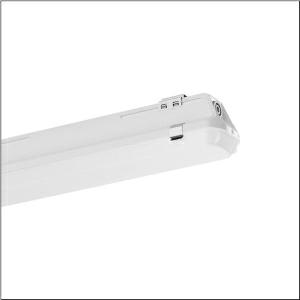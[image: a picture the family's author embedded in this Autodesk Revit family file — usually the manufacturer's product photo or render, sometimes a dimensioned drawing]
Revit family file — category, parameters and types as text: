
# Revit family: monsun_r__21_parking_51fg20dp440b_2f1b
name_source: partatom
category: Lighting Fixtures
units: mm (PartAtom-declared; Revit-internal decimal feet)

## family parameters
Cut with Voids When Loaded = No
Host = Face
Light Source = No
Part Type = Normal
Room Calculation Point = No
Round Connector Dimension = Use Diameter
Shared = No

## types (1)
- --- (1 x LED, 4810 lm, 34.4 W, 4000K)
    Apparent Load = 34 VA
    CIE Flux Codes = 45 75 93 94 100
    Color Rendering = 80
    Color Temperature = 4000K
    Default Elevation = 1800 mm
    Description = Monsun® 21 parking, damp-proof luminaire, chain hanger, primary optical cover: enclosure, of PC, light emission: direct distribution, primary light characteristic: symmetric, installation type: suspended mounting, surface-mounted, horizontal mounting, vertical mounting, LED, rated luminous flux: 4.810lm, luminous efficacy: 140lm/W, light colour: 840, colour temperature: 4000K, control gear: ECG DALI, with terminal, 5-pole, max. 2.5mm², mains connection: 220..240V, AC, 50/60Hz, rated input power: 34W, housing, of glass-fibre reinforced polyester, uncoated, bright grey, incl. chain hanger, length: 1.590mm, width: 90mm, height: 88mm, clip for enclosure, of stainless steel (V2A), ceiling mounting element, of stainless steel (V2A), chain hanger, of stainless steel (V2A), protection rating (complete): IP66, insulation class (complete): insulation class I (protective earthing), certification: CE, ENEC, VDE, UKCA, protection symbol: D, impact resistance: IK08, permissible operating ambient temperature: -25..+35°C, standard: EN 50419, EN 60598-2-1, corresponds to IFS (International Featured Standards) requirements for safety and quality in the food industry, for indoor or canopied outdoor use, no direct snow, no direct sun, no direct rain, contact your sales advisor before using the luminaires in applications with unclear chemical exposure, large temperature fluctuations or condensation-forming humidity, LABS conformity tested according to VDMA 24364:2018-05, packaging unit: 1 piece
    Height = 89 mm
    Lamp = 1 x LED
    Lamp Light Flux = 4810 lm
    Lamp Power = 34.4 W
    Lamp count = 1
    Length = 1590 mm
    Luminous efficacy = 140 lm/W
    Manufacturer = Siteco
    ModVariant = No
    Model = 51FG20DP440B
    Mounting Place = Ceiling
    Mounting Type = Surface mounted
    Number of Poles = 1
    OnlyDefault = Yes
    Power Factor = 1
    Product Name = Monsun® 21 parking
    Product group = damp-proof luminaire
    ProductGroupID = 300
    Protection Class = Protection class I
    Protection Degree = IP 66
    RLX_Detail_Level = 1
    RLX_Emergency_Light_Flux = 0 lm
    RLX_Emergency_Type = 0
    RLX_Emergency_Type_DB = No
    RlxData = <blob elided: 92781 chars, md5=301b6633>
    Socket = socket
    Standby Power = 0 W
    System Light Flux = 4810 lm
    System Power = 34 W
    Type Comments = factory setting: luminous flux: 100 % | dim-lin: 254 | 228 mA
    Type Image = l_1006717.jpg
    URL = http://relux.com
    VarID = @adj_134229
    Voltage = 0 V
    Weight = 0.00 kg
    Width = 90 mm

## geometry (parser evidence)
native form markers: Blend x4, Sweep x13
no freeform markers — native parametric forms only
